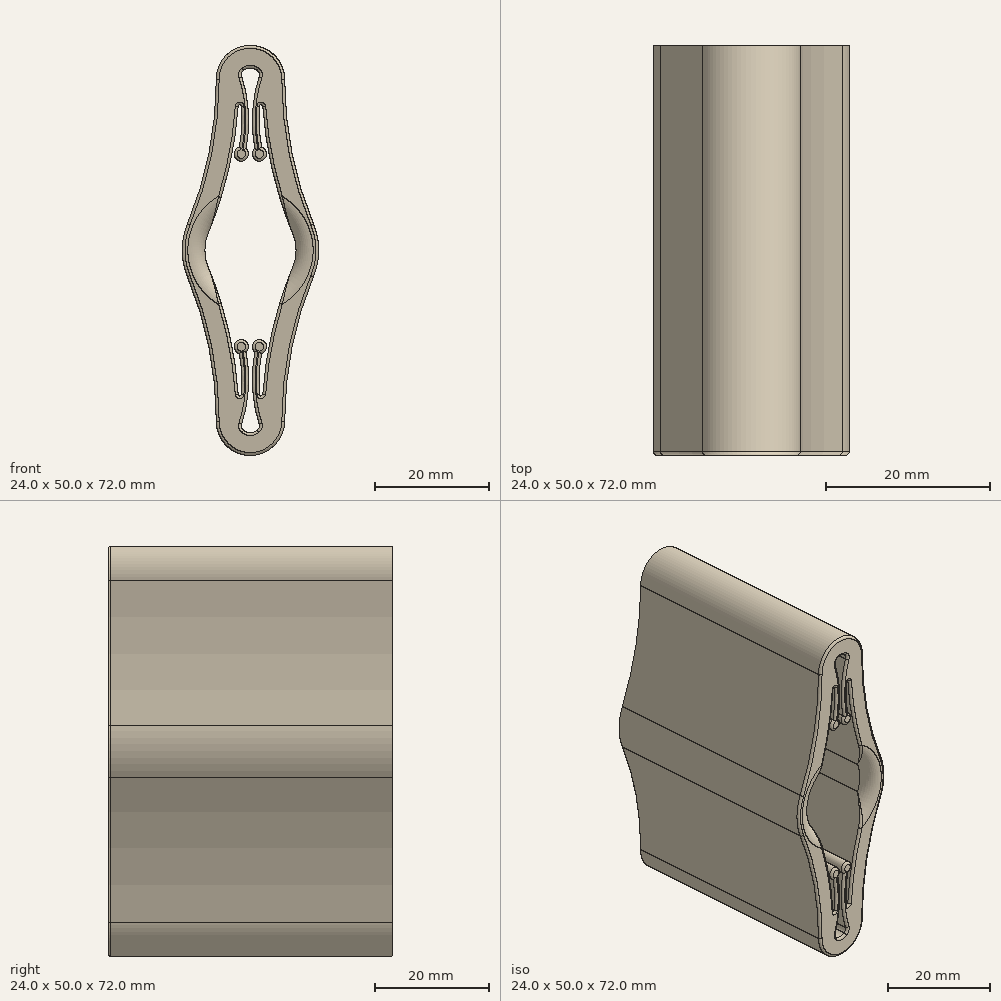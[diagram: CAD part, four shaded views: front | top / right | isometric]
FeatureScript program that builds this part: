
annotation { "Feature Type Name" : "Feature", "Feature Type Description" : "" }
export const myFeature = defineFeature(function(context is Context, id is Id, definition is map)
    precondition{}
    {
        {
            var Q0;
            Q0=qCreatedBy(makeId("Front.planeOp"),FACE);
            var sketch = newSketch(context, id + "F0", { "sketchPlane" : qUnion([Q0])});
            skLineSegment(sketch, "E0", {"start": v(0, 0) * mm, "end": v(0, 4) * mm, "construction": true});
            skArc(sketch, "E1", {"start": v(-1.16, 2.37) * mm, "mid": v(0, 2) * mm, "end": v(1.16, 2.37) * mm});
            skLineSegment(sketch, "E2", {"start": v(0, 4) * mm, "end": v(0, 64) * mm, "construction": true});
            skArc(sketch, "E3", {"start": v(1.16, 65.63) * mm, "mid": v(0, 66) * mm, "end": v(-1.16, 65.63) * mm});
            skArc(sketch, "E4", {"start": v(-7.38, 37.08) * mm, "mid": v(-8, 34) * mm, "end": v(-7.38, 30.92) * mm});
            skLineSegment(sketch, "E5", {"start": v(-2, 64) * mm, "end": v(-2, 74) * mm, "construction": true});
            skArc(sketch, "E6", {"start": v(-7.38, 37.08) * mm, "mid": v(-3.86, 47.99) * mm, "end": v(-2.16, 59.33) * mm});
            skLineSegment(sketch, "E7", {"start": v(-2, 4) * mm, "end": v(-2, -6) * mm, "construction": true});
            skArc(sketch, "E8", {"start": v(-2.16, 8.67) * mm, "mid": v(-3.86, 20.01) * mm, "end": v(-7.38, 30.92) * mm});
            skArc(sketch, "E9.MirrorCS", {"start": v(7.38, 37.08) * mm, "mid": v(3.86, 47.99) * mm, "end": v(2.16, 59.33) * mm});
            skArc(sketch, "E10.MirrorCS", {"start": v(7.38, 37.08) * mm, "mid": v(8, 34) * mm, "end": v(7.38, 30.92) * mm});
            skArc(sketch, "E11.MirrorCS", {"start": v(2.16, 8.67) * mm, "mid": v(3.86, 20.01) * mm, "end": v(7.38, 30.92) * mm});
            skArc(sketch, "E12.0", {"start": v(-6, 4) * mm, "mid": v(-7.28, 16.94) * mm, "end": v(-11.08, 29.38) * mm});
            skArc(sketch, "E12.1", {"start": v(-11.08, 38.62) * mm, "mid": v(-12, 34) * mm, "end": v(-11.08, 29.38) * mm});
            skArc(sketch, "E12.2", {"start": v(-11.08, 38.62) * mm, "mid": v(-7.28, 51.06) * mm, "end": v(-6, 64) * mm});
            skArc(sketch, "E12.3", {"start": v(6, 4) * mm, "mid": v(7.28, 16.94) * mm, "end": v(11.08, 29.38) * mm});
            skArc(sketch, "E12.4", {"start": v(11.08, 38.62) * mm, "mid": v(12, 34) * mm, "end": v(11.08, 29.38) * mm});
            skArc(sketch, "E12.5", {"start": v(11.08, 38.62) * mm, "mid": v(7.28, 51.06) * mm, "end": v(6, 64) * mm});
            skArc(sketch, "E12.6", {"start": v(6, 64) * mm, "mid": v(0, 70) * mm, "end": v(-6, 64) * mm});
            skArc(sketch, "E13", {"start": v(-6, 4) * mm, "mid": v(0, -2) * mm, "end": v(6, 4) * mm});
            skCircle(sketch, "E14", {"center": v(0, 34) * mm, "radius": 17 * mm, "construction": true});
            skArc(sketch, "E15", {"start": v(-0.78, 16.13) * mm, "mid": v(-1.86, 18.3) * mm, "end": v(-1.96, 15.88) * mm});
            skLineSegment(sketch, "E16", {"start": v(-1.6, 17.08) * mm, "end": v(0, 34) * mm, "construction": true});
            skArc(sketch, "E17", {"start": v(-2, 4) * mm, "mid": v(-0.93, 10.51) * mm, "end": v(-1.6, 17.08) * mm, "construction": true});
            skArc(sketch, "E18.0", {"start": v(-1.53, 3.49) * mm, "mid": v(-0.36, 9.76) * mm, "end": v(-0.78, 16.13) * mm});
            skArc(sketch, "E19.0", {"start": v(-1.66, 8.66) * mm, "mid": v(-1.54, 12.28) * mm, "end": v(-1.96, 15.88) * mm});
            skArc(sketch, "E20.MirrorCS", {"start": v(1.53, 3.49) * mm, "mid": v(0.36, 9.76) * mm, "end": v(0.78, 16.13) * mm});
            skArc(sketch, "E21.MirrorCS", {"start": v(1.66, 8.66) * mm, "mid": v(1.54, 12.28) * mm, "end": v(1.96, 15.88) * mm});
            skArc(sketch, "E22.MirrorCS", {"start": v(0.78, 16.13) * mm, "mid": v(1.86, 18.3) * mm, "end": v(1.96, 15.88) * mm});
            skPoint(sketch, "E23.orphan", {"position": v(2, 4) * mm});
            skLineSegment(sketch, "E24", {"start": v(0, 34) * mm, "end": v(8, 34) * mm, "construction": true});
            skArc(sketch, "E25.MirrorCS", {"start": v(-1.66, 59.34) * mm, "mid": v(-1.54, 55.72) * mm, "end": v(-1.96, 52.12) * mm});
            skArc(sketch, "E26.MirrorCS", {"start": v(-0.78, 51.87) * mm, "mid": v(-1.86, 49.7) * mm, "end": v(-1.96, 52.12) * mm});
            skArc(sketch, "E27.MirrorCS", {"start": v(-1.53, 64.51) * mm, "mid": v(-0.36, 58.24) * mm, "end": v(-0.78, 51.87) * mm});
            skArc(sketch, "E28.MirrorCS", {"start": v(1.53, 64.51) * mm, "mid": v(0.36, 58.24) * mm, "end": v(0.78, 51.87) * mm});
            skArc(sketch, "E29.MirrorCS", {"start": v(1.66, 59.34) * mm, "mid": v(1.54, 55.72) * mm, "end": v(1.96, 52.12) * mm});
            skArc(sketch, "E30.MirrorCS", {"start": v(0.78, 51.87) * mm, "mid": v(1.86, 49.7) * mm, "end": v(1.96, 52.12) * mm});
            skPoint(sketch, "E31.orphan", {"position": v(2, 64) * mm});
            skPoint(sketch, "E32.visualSharp", {"position": v(-2.04, 61.73) * mm});
            skArc(sketch, "E32.filletArc", {"start": v(-1.66, 59.34) * mm, "mid": v(-1.91, 59.56) * mm, "end": v(-2.16, 59.33) * mm});
            skPoint(sketch, "E33.visualSharp", {"position": v(2.04, 61.73) * mm});
            skArc(sketch, "E33.filletArc", {"start": v(2.16, 59.33) * mm, "mid": v(1.91, 59.56) * mm, "end": v(1.66, 59.34) * mm});
            skPoint(sketch, "E34.visualSharp", {"position": v(-2.04, 6.27) * mm});
            skArc(sketch, "E34.filletArc", {"start": v(-2.16, 8.67) * mm, "mid": v(-1.91, 8.44) * mm, "end": v(-1.66, 8.66) * mm});
            skPoint(sketch, "E35.visualSharp", {"position": v(2.04, 6.27) * mm});
            skArc(sketch, "E35.filletArc", {"start": v(1.66, 8.66) * mm, "mid": v(1.91, 8.44) * mm, "end": v(2.16, 8.67) * mm});
            skPoint(sketch, "E36.visualSharp", {"position": v(1.7, 2.96) * mm});
            skArc(sketch, "E36.filletArc", {"start": v(1.16, 2.37) * mm, "mid": v(1.53, 2.87) * mm, "end": v(1.53, 3.49) * mm});
            skPoint(sketch, "E37.visualSharp", {"position": v(-1.7, 2.96) * mm});
            skArc(sketch, "E37.filletArc", {"start": v(-1.53, 3.49) * mm, "mid": v(-1.53, 2.87) * mm, "end": v(-1.16, 2.37) * mm});
            skPoint(sketch, "E38.visualSharp", {"position": v(-1.7, 65.04) * mm});
            skArc(sketch, "E38.filletArc", {"start": v(-1.16, 65.63) * mm, "mid": v(-1.53, 65.13) * mm, "end": v(-1.53, 64.51) * mm});
            skPoint(sketch, "E39.visualSharp", {"position": v(1.7, 65.04) * mm});
            skArc(sketch, "E39.filletArc", {"start": v(1.53, 64.51) * mm, "mid": v(1.53, 65.13) * mm, "end": v(1.16, 65.63) * mm});
            skSolve(sketch);
        }
        {
            var Q0;
            Q0 = qSketchRegion(id + "F0", true);
            extrude(context, id + "F1", {"entities" : qUnion([Q0]), "oppositeDirection" : true, "depth" : 50 * mm});
        }
        {
            var Q0;
            Q0=makeQuery(id+"F1.opExtrude","CAP_EDGE",EDGE,{"disambiguationData":[OSD([sQuery(id+"F0.wireOp",EDGE,"E4")])],"isStart":true});
            var Q1;
            Q1=makeQuery(id+"F1.opExtrude","CAP_EDGE",EDGE,{"disambiguationData":[OSD([sQuery(id+"F0.wireOp",EDGE,"E10.MirrorCS")])],"isStart":true});
            fillet(context, id + "F2", {"entities" : qUnion([Q0, Q1]), "radius" : 3 * mm, "allowEdgeOverflow" : false});
        }
        {
            var Q0;
            Q0=makeQuery(id+"F1.opExtrude","CAP_EDGE",EDGE,{"disambiguationData":[OSD([sQuery(id+"F0.wireOp",EDGE,"E26.MirrorCS")])],"isStart":true});
            var Q1;
            Q1=makeQuery(id+"F1.opExtrude","CAP_EDGE",EDGE,{"disambiguationData":[OSD([sQuery(id+"F0.wireOp",EDGE,"E25.MirrorCS")])],"isStart":true});
            var Q2;
            Q2=makeQuery(id+"F1.opExtrude","CAP_EDGE",EDGE,{"disambiguationData":[OSD([sQuery(id+"F0.wireOp",EDGE,"E27.MirrorCS")])],"isStart":true});
            var Q3;
            Q3=makeQuery(id+"F1.opExtrude","CAP_EDGE",EDGE,{"disambiguationData":[OSD([sQuery(id+"F0.wireOp",EDGE,"E6")])],"isStart":true});
            var Q4;
            Q4=makeQuery(id+"F1.opExtrude","CAP_EDGE",EDGE,{"disambiguationData":[OSD([sQuery(id+"F0.wireOp",EDGE,"E3")])],"isStart":true});
            var Q5;
            Q5=makeQuery(id+"F1.opExtrude","CAP_EDGE",EDGE,{"disambiguationData":[OSD([sQuery(id+"F0.wireOp",EDGE,"E28.MirrorCS")])],"isStart":true});
            var Q6;
            Q6=makeQuery(id+"F1.opExtrude","CAP_EDGE",EDGE,{"disambiguationData":[OSD([sQuery(id+"F0.wireOp",EDGE,"E30.MirrorCS")])],"isStart":true});
            var Q7;
            Q7=makeQuery(id+"F1.opExtrude","CAP_EDGE",EDGE,{"disambiguationData":[OSD([sQuery(id+"F0.wireOp",EDGE,"E29.MirrorCS")])],"isStart":true});
            var Q8;
            Q8=makeQuery(id+"F1.opExtrude","CAP_EDGE",EDGE,{"disambiguationData":[OSD([sQuery(id+"F0.wireOp",EDGE,"E9.MirrorCS")])],"isStart":true});
            var Q9;
            Q9=makeQuery(id+"F1.opExtrude","CAP_EDGE",EDGE,{"disambiguationData":[OSD([sQuery(id+"F0.wireOp",EDGE,"E8")])],"isStart":true});
            var Q10;
            Q10=makeQuery(id+"F1.opExtrude","CAP_EDGE",EDGE,{"disambiguationData":[OSD([sQuery(id+"F0.wireOp",EDGE,"E19.0")])],"isStart":true});
            var Q11;
            Q11=makeQuery(id+"F1.opExtrude","CAP_FACE",FACE,{"disambiguationData":[OSD([sQuery(id+"F0.wireOp",EDGE,"E1"),sQuery(id+"F0.wireOp",EDGE,"E3"),sQuery(id+"F0.wireOp",EDGE,"E4"),sQuery(id+"F0.wireOp",EDGE,"E6"),sQuery(id+"F0.wireOp",EDGE,"E8"),sQuery(id+"F0.wireOp",EDGE,"E9.MirrorCS"),sQuery(id+"F0.wireOp",EDGE,"E10.MirrorCS"),sQuery(id+"F0.wireOp",EDGE,"E11.MirrorCS"),sQuery(id+"F0.wireOp",EDGE,"E12.0"),sQuery(id+"F0.wireOp",EDGE,"E12.1"),sQuery(id+"F0.wireOp",EDGE,"E12.2"),sQuery(id+"F0.wireOp",EDGE,"E12.3"),sQuery(id+"F0.wireOp",EDGE,"E12.4"),sQuery(id+"F0.wireOp",EDGE,"E12.5"),sQuery(id+"F0.wireOp",EDGE,"E12.6"),sQuery(id+"F0.wireOp",EDGE,"E13"),sQuery(id+"F0.wireOp",EDGE,"E15"),sQuery(id+"F0.wireOp",EDGE,"E18.0"),sQuery(id+"F0.wireOp",EDGE,"E19.0"),sQuery(id+"F0.wireOp",EDGE,"E20.MirrorCS"),sQuery(id+"F0.wireOp",EDGE,"E21.MirrorCS"),sQuery(id+"F0.wireOp",EDGE,"E22.MirrorCS"),sQuery(id+"F0.wireOp",EDGE,"E25.MirrorCS"),sQuery(id+"F0.wireOp",EDGE,"E26.MirrorCS"),sQuery(id+"F0.wireOp",EDGE,"E27.MirrorCS"),sQuery(id+"F0.wireOp",EDGE,"E28.MirrorCS"),sQuery(id+"F0.wireOp",EDGE,"E29.MirrorCS"),sQuery(id+"F0.wireOp",EDGE,"E30.MirrorCS")])],"isStart":true});
            fillet(context, id + "F3", {"entities" : qUnion([Q0, Q1, Q2, Q3, Q4, Q5, Q6, Q7, Q8, Q9, Q10, Q11]), "radius" : 0.5 * mm, "tangentPropagation" : true, "allowEdgeOverflow" : false});
        }
    });
